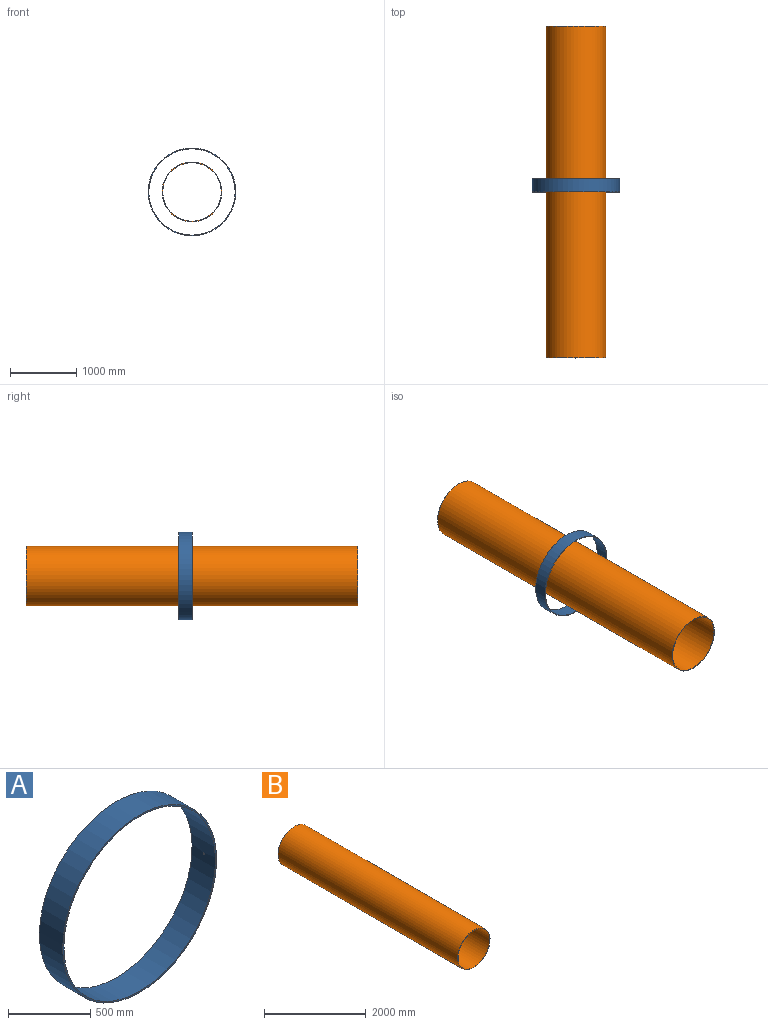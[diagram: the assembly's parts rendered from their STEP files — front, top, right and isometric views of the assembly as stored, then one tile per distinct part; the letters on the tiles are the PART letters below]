
ASSEMBLY  parts=2 mates=1
PART A: 5 faces, bbox 1320x200x1320 mm
  f0: cylinder r=650mm len=1300mm, axis (0,1,0), area 816727.2mm2, adj f2,f3,f4
  f1: cylinder r=660mm len=1320mm, axis (0,1,0), area 829293.7mm2, adj f2,f3,f4
  f2: plane 1320x1320mm, normal (0,-1,0), area 41154.9mm2, adj f0,f1
  f3: plane 1320x1320mm, normal (0,1,0), area 41154.9mm2, adj f0,f1
  f4: cylinder r=5.5mm len=11mm, axis (-1,0,0), area 345.6mm2, adj f0,f1
PART B: 4 faces, bbox 900x5000x900 mm
  f0: cylinder r=440mm len=5000mm, axis (0,1,0), area 13823007.7mm2, adj f2,f3
  f1: cylinder r=450mm len=5000mm, axis (0,1,0), area 14137166.9mm2, adj f2,f3
  f2: plane 900x900mm, normal (0,-1,0), area 27960.2mm2, adj f0,f1
  f3: plane 900x900mm, normal (0,1,0), area 27960.2mm2, adj f0,f1
PLACE A t=(-1635.17,-1323.26,-718.79)mm
PLACE B t=(-1635.17,976.74,-718.79)mm
MATE cylindrical A.f0 <-> B.f1  axis (0,-1,0) through (-1635.17,-1523.26,-718.79)mm
